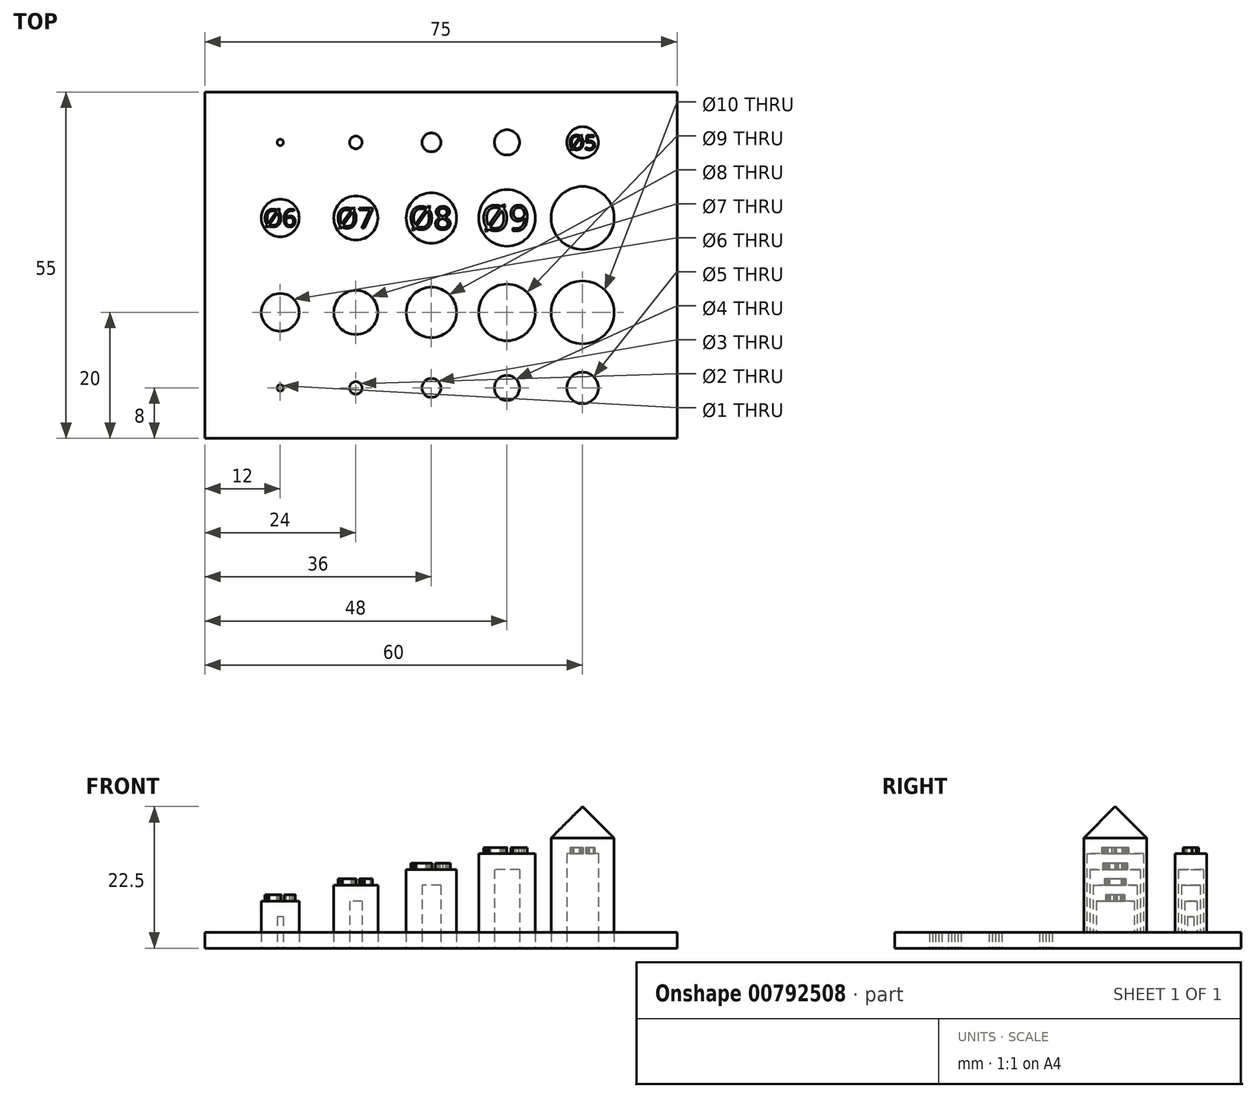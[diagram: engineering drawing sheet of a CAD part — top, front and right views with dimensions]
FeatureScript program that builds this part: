
annotation { "Feature Type Name" : "Feature", "Feature Type Description" : "" }
export const myFeature = defineFeature(function(context is Context, id is Id, definition is map)
    precondition{}
    {
        {
            var Q0;
            Q0=qCreatedBy(makeId("Top.planeOp"),FACE);
            var sketch = newSketch(context, id + "F0", { "sketchPlane" : qUnion([Q0])});
            skLineSegment(sketch, "E0.bottom", {"start": v(-37.5, 27.5) * mm, "end": v(37.5, 27.5) * mm});
            skLineSegment(sketch, "E0.top", {"start": v(-37.5, -27.5) * mm, "end": v(37.5, -27.5) * mm});
            skLineSegment(sketch, "E0.left", {"start": v(-37.5, 27.5) * mm, "end": v(-37.5, -27.5) * mm});
            skLineSegment(sketch, "E0.right", {"start": v(37.5, 27.5) * mm, "end": v(37.5, -27.5) * mm});
            skPoint(sketch, "E0.middle", {"position": v(0, 0) * mm});
            skCircle(sketch, "E1", {"center": v(-25.5, 19.5) * mm, "radius": 0.5 * mm});
            skCircle(sketch, "E2", {"center": v(-13.5, 19.5) * mm, "radius": 1 * mm});
            skCircle(sketch, "E3", {"center": v(-1.5, 19.5) * mm, "radius": 1.5 * mm});
            skCircle(sketch, "E4", {"center": v(10.5, 19.5) * mm, "radius": 2 * mm});
            skCircle(sketch, "E5", {"center": v(22.5, 19.5) * mm, "radius": 2.5 * mm});
            skCircle(sketch, "E6", {"center": v(-25.5, 7.5) * mm, "radius": 3 * mm});
            skCircle(sketch, "E7", {"center": v(-13.5, 7.5) * mm, "radius": 3.5 * mm});
            skCircle(sketch, "E8", {"center": v(-1.5, 7.5) * mm, "radius": 4 * mm});
            skCircle(sketch, "E9", {"center": v(10.5, 7.5) * mm, "radius": 4.5 * mm});
            skCircle(sketch, "E10", {"center": v(22.5, 7.5) * mm, "radius": 5 * mm});
            skLineSegment(sketch, "E11", {"start": v(-37.5, 0) * mm, "end": v(37.5, 0) * mm, "construction": true});
            skCircle(sketch, "E12.MirrorC", {"center": v(22.5, -7.5) * mm, "radius": 5 * mm});
            skCircle(sketch, "E13.MirrorC", {"center": v(10.5, -7.5) * mm, "radius": 4.5 * mm});
            skCircle(sketch, "E14.MirrorC", {"center": v(-1.5, -7.5) * mm, "radius": 4 * mm});
            skCircle(sketch, "E15.MirrorC", {"center": v(-13.5, -7.5) * mm, "radius": 3.5 * mm});
            skCircle(sketch, "E16.MirrorC", {"center": v(-25.5, -7.5) * mm, "radius": 3 * mm});
            skCircle(sketch, "E17.MirrorC", {"center": v(22.5, -19.5) * mm, "radius": 2.5 * mm});
            skCircle(sketch, "E18.MirrorC", {"center": v(10.5, -19.5) * mm, "radius": 2 * mm});
            skCircle(sketch, "E19.MirrorC", {"center": v(-1.5, -19.5) * mm, "radius": 1.5 * mm});
            skCircle(sketch, "E20.MirrorC", {"center": v(-13.5, -19.5) * mm, "radius": 1 * mm});
            skCircle(sketch, "E21.MirrorC", {"center": v(-25.5, -19.5) * mm, "radius": 0.5 * mm});
            skSolve(sketch);
        }
        {
            var Q0;
            Q0=makeQuery(id+"F0.imprint","IMPRINT",FACE,{"disambiguationData":[TD([[makeQuery(id+"F0.imprint","IMPRINT",EDGE,{"derivedFrom":sQuery(id+"F0.wireOp",EDGE,"E0.bottom")}),-1.0]])]});
            extrude(context, id + "F1", {"entities" : qUnion([Q0]), "depth" : 2.5 * mm, "offsetDistance" : 25 * mm});
        }
        {
            var Q0;
            Q0=makeQuery(id+"F0.imprint","IMPRINT",FACE,{"disambiguationData":[TD([[makeQuery(id+"F0.imprint","IMPRINT",EDGE,{"derivedFrom":sQuery(id+"F0.wireOp",EDGE,"E1")}),1.0]])]});
            extrude(context, id + "F2", {"entities" : qUnion([Q0]), "operationType" : NewBodyOperationType.ADD, "depth" : 5 * mm, "offsetDistance" : 25 * mm});
        }
        {
            var Q0;
            Q0=makeQuery(id+"F0.imprint","IMPRINT",FACE,{"disambiguationData":[TD([[makeQuery(id+"F0.imprint","IMPRINT",EDGE,{"derivedFrom":sQuery(id+"F0.wireOp",EDGE,"E2")}),1.0]])]});
            extrude(context, id + "F3", {"entities" : qUnion([Q0]), "operationType" : NewBodyOperationType.ADD, "depth" : 7.5 * mm, "offsetDistance" : 25 * mm});
        }
        {
            var Q0;
            Q0=makeQuery(id+"F0.imprint","IMPRINT",FACE,{"disambiguationData":[TD([[makeQuery(id+"F0.imprint","IMPRINT",EDGE,{"derivedFrom":sQuery(id+"F0.wireOp",EDGE,"E3")}),1.0]])]});
            extrude(context, id + "F4", {"entities" : qUnion([Q0]), "operationType" : NewBodyOperationType.ADD, "depth" : 10 * mm, "offsetDistance" : 25 * mm});
        }
        {
            var Q0;
            Q0=makeQuery(id+"F0.imprint","IMPRINT",FACE,{"disambiguationData":[TD([[makeQuery(id+"F0.imprint","IMPRINT",EDGE,{"derivedFrom":sQuery(id+"F0.wireOp",EDGE,"E4")}),1.0]])]});
            extrude(context, id + "F5", {"entities" : qUnion([Q0]), "operationType" : NewBodyOperationType.ADD, "depth" : 12.5 * mm, "offsetDistance" : 25 * mm});
        }
        {
            var Q0;
            Q0=makeQuery(id+"F0.imprint","IMPRINT",FACE,{"disambiguationData":[TD([[makeQuery(id+"F0.imprint","IMPRINT",EDGE,{"derivedFrom":sQuery(id+"F0.wireOp",EDGE,"E5")}),1.0]])]});
            extrude(context, id + "F6", {"entities" : qUnion([Q0]), "operationType" : NewBodyOperationType.ADD, "depth" : 15 * mm, "offsetDistance" : 25 * mm});
        }
        {
            var Q0;
            Q0=makeQuery(id+"F0.imprint","IMPRINT",FACE,{"disambiguationData":[TD([[makeQuery(id+"F0.imprint","IMPRINT",EDGE,{"derivedFrom":sQuery(id+"F0.wireOp",EDGE,"E6")}),1.0]])]});
            extrude(context, id + "F7", {"entities" : qUnion([Q0]), "operationType" : NewBodyOperationType.ADD, "depth" : 7.5 * mm, "offsetDistance" : 25 * mm});
        }
        {
            var Q0;
            Q0=makeQuery(id+"F0.imprint","IMPRINT",FACE,{"disambiguationData":[TD([[makeQuery(id+"F0.imprint","IMPRINT",EDGE,{"derivedFrom":sQuery(id+"F0.wireOp",EDGE,"E7")}),1.0]])]});
            extrude(context, id + "F8", {"entities" : qUnion([Q0]), "operationType" : NewBodyOperationType.ADD, "depth" : 10 * mm, "offsetDistance" : 25 * mm});
        }
        {
            var Q0;
            Q0=makeQuery(id+"F0.imprint","IMPRINT",FACE,{"disambiguationData":[TD([[makeQuery(id+"F0.imprint","IMPRINT",EDGE,{"derivedFrom":sQuery(id+"F0.wireOp",EDGE,"E8")}),1.0]])]});
            extrude(context, id + "F9", {"entities" : qUnion([Q0]), "operationType" : NewBodyOperationType.ADD, "depth" : 12.5 * mm, "offsetDistance" : 25 * mm});
        }
        {
            var Q0;
            Q0=makeQuery(id+"F0.imprint","IMPRINT",FACE,{"disambiguationData":[TD([[makeQuery(id+"F0.imprint","IMPRINT",EDGE,{"derivedFrom":sQuery(id+"F0.wireOp",EDGE,"E9")}),1.0]])]});
            extrude(context, id + "F10", {"entities" : qUnion([Q0]), "operationType" : NewBodyOperationType.ADD, "depth" : 15 * mm, "offsetDistance" : 25 * mm});
        }
        {
            var Q0;
            Q0=makeQuery(id+"F0.imprint","IMPRINT",FACE,{"disambiguationData":[TD([[makeQuery(id+"F0.imprint","IMPRINT",EDGE,{"derivedFrom":sQuery(id+"F0.wireOp",EDGE,"E10")}),1.0]])]});
            extrude(context, id + "F11", {"entities" : qUnion([Q0]), "operationType" : NewBodyOperationType.ADD, "depth" : 22.5 * mm, "offsetDistance" : 25 * mm});
        }
        {
            var Q0;
            Q0=makeQuery(id+"F11.opExtrude","CAP_EDGE",EDGE,{"disambiguationData":[OSD([sQuery(id+"F0.wireOp",EDGE,"E10")])],"isStart":false});
            chamfer(context, id + "F12", {"entities" : qUnion([Q0]), "width" : 5 * mm, "tangentPropagation" : true});
        }
        {
            var Q0;
            Q0=makeQuery(id+"F10.opExtrude","CAP_FACE",FACE,{"disambiguationData":[OSD([sQuery(id+"F0.wireOp",EDGE,"E9")])],"isStart":false});
            var sketch = newSketch(context, id + "F13", { "sketchPlane" : qUnion([Q0])});
            skText(sketch, "E22", { "text": "Ø9", "fontName": "OpenSans-Regular.ttf"});
            const initialGuessF13  = {"E22": [0.00647, 0.0055, 1, 0, 0.00402]};
            skSetInitialGuess(sketch, initialGuessF13);
            skSolve(sketch);
        }
        {
            var Q0;
            Q0=makeQuery(id+"F13.imprint","IMPRINT",FACE,{"disambiguationData":[TD([[makeQuery(id+"F13.imprint","IMPRINT",EDGE,{"derivedFrom":sQuery(id+"F13.wireOp",EDGE,"E22.sketch_text.stroke-0")}),-1.0]])]});
            var Q1;
            Q1=makeQuery(id+"F13.imprint","IMPRINT",FACE,{"disambiguationData":[TD([[makeQuery(id+"F13.imprint","IMPRINT",EDGE,{"derivedFrom":sQuery(id+"F13.wireOp",EDGE,"E22.sketch_text.stroke-24")}),-1.0]])]});
            extrude(context, id + "F14", {"entities" : qUnion([Q0, Q1]), "operationType" : NewBodyOperationType.ADD, "depth" : 1 * mm, "offsetDistance" : 25 * mm});
        }
        {
            var Q0;
            Q0=makeQuery(id+"F9.opExtrude","CAP_FACE",FACE,{"disambiguationData":[OSD([sQuery(id+"F0.wireOp",EDGE,"E8")])],"isStart":false});
            var sketch = newSketch(context, id + "F15", { "sketchPlane" : qUnion([Q0])});
            skText(sketch, "E23", { "text": "Ø8", "fontName": "OpenSans-Regular.ttf"});
            const initialGuessF15  = {"E23": [-0.00506, 0.00568, 1, 0, 0.00364]};
            skSetInitialGuess(sketch, initialGuessF15);
            skSolve(sketch);
        }
        {
            var Q0;
            Q0 = qSketchRegion(id + "F15", true);
            extrude(context, id + "F16", {"entities" : qUnion([Q0]), "operationType" : NewBodyOperationType.ADD, "depth" : 1 * mm, "offsetDistance" : 25 * mm});
        }
        {
            var Q0;
            Q0=makeQuery(id+"F8.opExtrude","CAP_FACE",FACE,{"disambiguationData":[OSD([sQuery(id+"F0.wireOp",EDGE,"E7")])],"isStart":false});
            var sketch = newSketch(context, id + "F17", { "sketchPlane" : qUnion([Q0])});
            skText(sketch, "E24", { "text": "Ø7", "fontName": "OpenSans-Regular.ttf"});
            const initialGuessF17  = {"E24": [-0.01662, 0.0059, 1, 0, 0.00319]};
            skSetInitialGuess(sketch, initialGuessF17);
            skSolve(sketch);
        }
        {
            var Q0;
            Q0 = qSketchRegion(id + "F17", true);
            extrude(context, id + "F18", {"entities" : qUnion([Q0]), "operationType" : NewBodyOperationType.ADD, "depth" : 1 * mm, "offsetDistance" : 25 * mm});
        }
        {
            var Q0;
            Q0=makeQuery(id+"F7.opExtrude","CAP_FACE",FACE,{"disambiguationData":[OSD([sQuery(id+"F0.wireOp",EDGE,"E6")])],"isStart":false});
            var sketch = newSketch(context, id + "F19", { "sketchPlane" : qUnion([Q0])});
            skText(sketch, "E25", { "text": "Ø6", "fontName": "OpenSans-Regular.ttf"});
            const initialGuessF19  = {"E25": [-0.02816, 0.0061, 1, 0, 0.00279]};
            skSetInitialGuess(sketch, initialGuessF19);
            skSolve(sketch);
        }
        {
            var Q0;
            Q0 = qSketchRegion(id + "F19", true);
            extrude(context, id + "F20", {"entities" : qUnion([Q0]), "operationType" : NewBodyOperationType.ADD, "depth" : 1 * mm, "offsetDistance" : 25 * mm});
        }
        {
            var Q0;
            Q0=makeQuery(id+"F6.opExtrude","CAP_FACE",FACE,{"disambiguationData":[OSD([sQuery(id+"F0.wireOp",EDGE,"E5")])],"isStart":false});
            var sketch = newSketch(context, id + "F21", { "sketchPlane" : qUnion([Q0])});
            skText(sketch, "E26", { "text": "Ø5", "fontName": "OpenSans-Regular.ttf"});
            const initialGuessF21  = {"E26": [0.02029, 0.01834, 1, 0, 0.00232]};
            skSetInitialGuess(sketch, initialGuessF21);
            skSolve(sketch);
        }
        {
            var Q0;
            Q0 = qSketchRegion(id + "F21", true);
            extrude(context, id + "F22", {"entities" : qUnion([Q0]), "operationType" : NewBodyOperationType.ADD, "depth" : 1 * mm, "offsetDistance" : 25 * mm});
        }
    });
